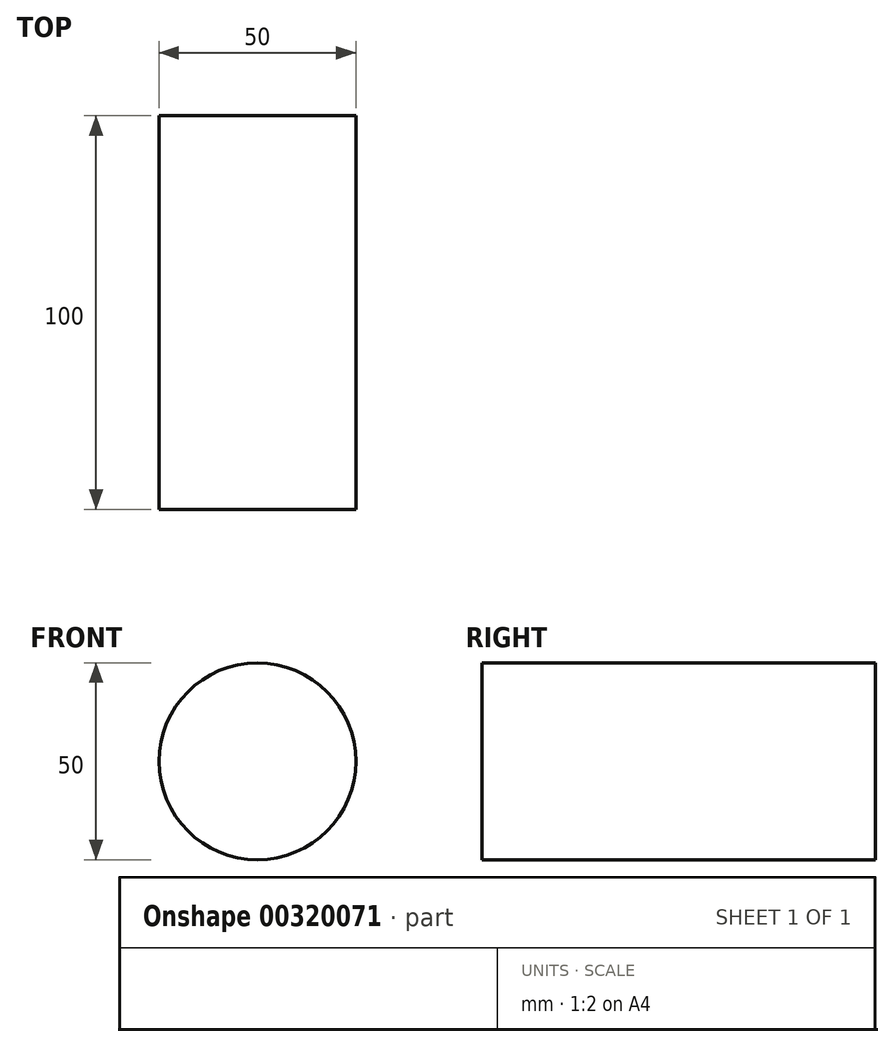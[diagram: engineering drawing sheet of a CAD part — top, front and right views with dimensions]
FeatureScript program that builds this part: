
annotation { "Feature Type Name" : "Feature", "Feature Type Description" : "" }
export const myFeature = defineFeature(function(context is Context, id is Id, definition is map)
    precondition{}
    {
        {
            var Q0;
            Q0=qCreatedBy(makeId("Front.planeOp"),FACE);
            var sketch = newSketch(context, id + "F0", { "sketchPlane" : qUnion([Q0])});
            skCircle(sketch, "E0", {"center": v(0, 0) * mm, "radius": 25 * mm});
            skSolve(sketch);
        }
        {
            var Q0;
            Q0 = qSketchRegion(id + "F0", true);
            extrude(context, id + "F1", {"entities" : qUnion([Q0]), "depth" : 100 * mm});
        }
    });
